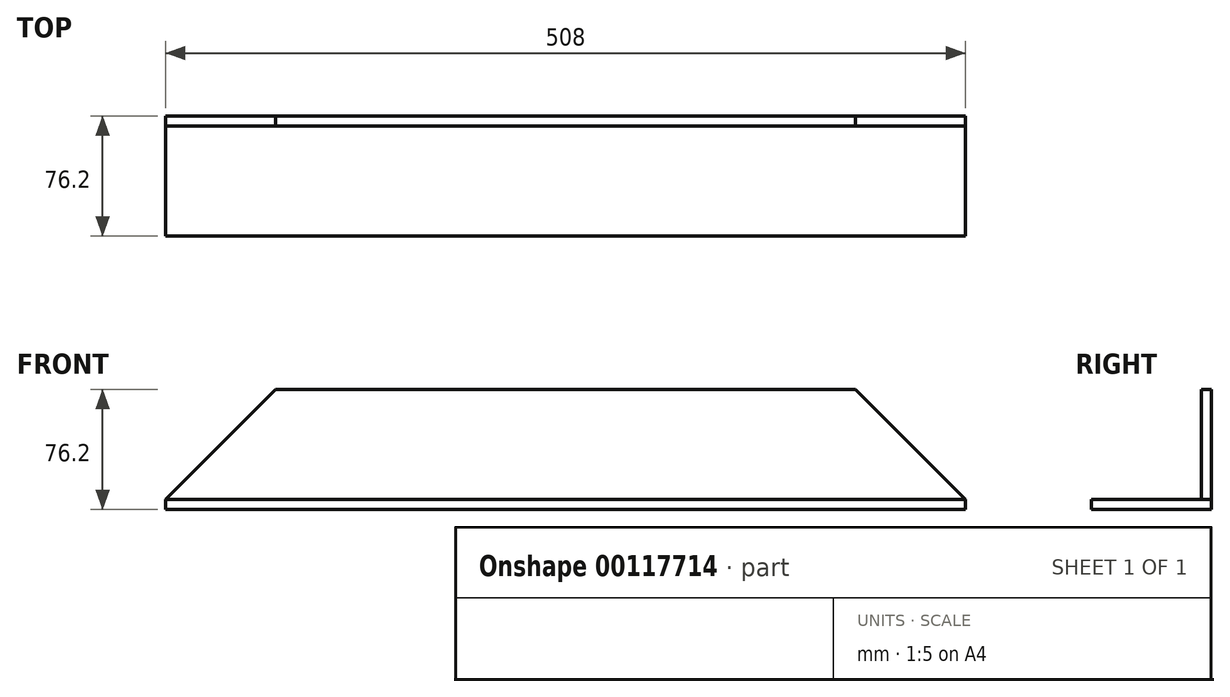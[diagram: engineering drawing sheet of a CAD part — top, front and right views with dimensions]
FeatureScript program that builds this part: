
annotation { "Feature Type Name" : "Feature", "Feature Type Description" : "" }
export const myFeature = defineFeature(function(context is Context, id is Id, definition is map)
    precondition{}
    {
        {
            var Q0;
            Q0=qCreatedBy(makeId("Front.planeOp"),FACE);
            var sketch = newSketch(context, id + "F0", { "sketchPlane" : qUnion([Q0])});
            skLineSegment(sketch, "E0", {"start": v(-287.03, -0.33) * mm, "end": v(220.97, -0.33) * mm});
            skLineSegment(sketch, "E1", {"start": v(151.12, 69.52) * mm, "end": v(-217.18, 69.52) * mm});
            skLineSegment(sketch, "E2", {"start": v(-287.03, -0.33) * mm, "end": v(-217.18, 69.52) * mm});
            skLineSegment(sketch, "E3", {"start": v(220.97, -0.33) * mm, "end": v(151.12, 69.52) * mm});
            skPoint(sketch, "E4.start.orphan", {"position": v(-287.03, 69.52) * mm});
            skLineSegment(sketch, "E5.top", {"start": v(-287.03, -6.68) * mm, "end": v(220.97, -6.68) * mm});
            skLineSegment(sketch, "E5.left", {"start": v(-287.03, -0.33) * mm, "end": v(-287.03, -6.68) * mm});
            skLineSegment(sketch, "E5.right", {"start": v(220.97, -0.33) * mm, "end": v(220.97, -6.68) * mm});
            skSolve(sketch);
        }
        {
            var Q0;
            Q0=makeQuery(id+"F0.imprint","IMPRINT",FACE,{"disambiguationData":[TD([[makeQuery(id+"F0.imprint","IMPRINT",EDGE,{"derivedFrom":sQuery(id+"F0.wireOp",EDGE,"E1")}),1.0]])]});
            extrude(context, id + "F1", {"entities" : qUnion([Q0]), "depth" : 6.35 * mm});
        }
        {
            var Q0;
            Q0=makeQuery(id+"F0.imprint","IMPRINT",FACE,{"disambiguationData":[TD([[makeQuery(id+"F0.imprint","IMPRINT",EDGE,{"derivedFrom":sQuery(id+"F0.wireOp",EDGE,"E0")}),-1.0]])]});
            extrude(context, id + "F2", {"entities" : qUnion([Q0]), "operationType" : NewBodyOperationType.ADD, "depth" : 76.2 * mm});
        }
    });
